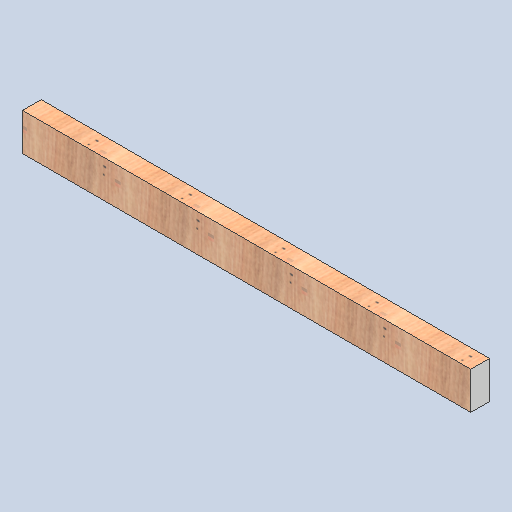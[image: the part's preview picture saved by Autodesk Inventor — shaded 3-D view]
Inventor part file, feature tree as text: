
AUTODESK INVENTOR PART (.ipt)
format: ipt  version: 2025 (Build 290162000, 162)  size: 146,432 bytes
history: native  units: in
note: dims shown in document units (in); Inventor stores cm internally (conversion verified against a paired STEP export)
features: other x3, sketch x2
ambient origin geometry x8: Origin, YZ Plane, XZ Plane, XY Plane, X Axis, Y Axis, Z Axis, Center Point
bodies: Solid1 (feature_tree)
feature tree (5):
  other  "2x4x48.ipt"
  other  "Solid1::2x4x48.ipt"
  other  "TaggingFeature1"
  sketch  "Sketch1"  dims[d0=0.3937in]
  sketch  "Sketch2"
